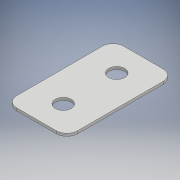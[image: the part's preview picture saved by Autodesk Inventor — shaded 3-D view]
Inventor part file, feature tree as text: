
AUTODESK INVENTOR PART (.ipt)
format: ipt  version: 2018 (Build 220112000, 112)  size: 120,320 bytes
history: native  units: mm
features: other x4, reference x3, extrude x1, fillet x1, sketch x1
ambient origin geometry x8: Origin, YZ Plane, XZ Plane, XY Plane, X Axis, Y Axis, Z Axis, Center Point
bodies: Solid1 (feature_tree)
feature tree (10):
  extrude  "Extrusion1"  Depth=2.0mm
  fillet  "Fillet1"  Radius=3.0mm
  sketch  "Sketch1"  dims[d0=20.0mm d1=5.0mm d2=3.0mm d4=3.0mm d5=0.5mm d6=0.0mm d7=2.0mm]
  reference  "Reference1"
  reference  "Reference2"
  reference  "Reference3"
  other  "<userpath>\OneDrive\Documents\Inventor\TSA\2018\Animatronics\Tortoise\Head\HeadAssembly.iam"
  other  "HeadAssembly.iam"
  other  "HeadTop:1"
  other  "HeadBottom:2"
